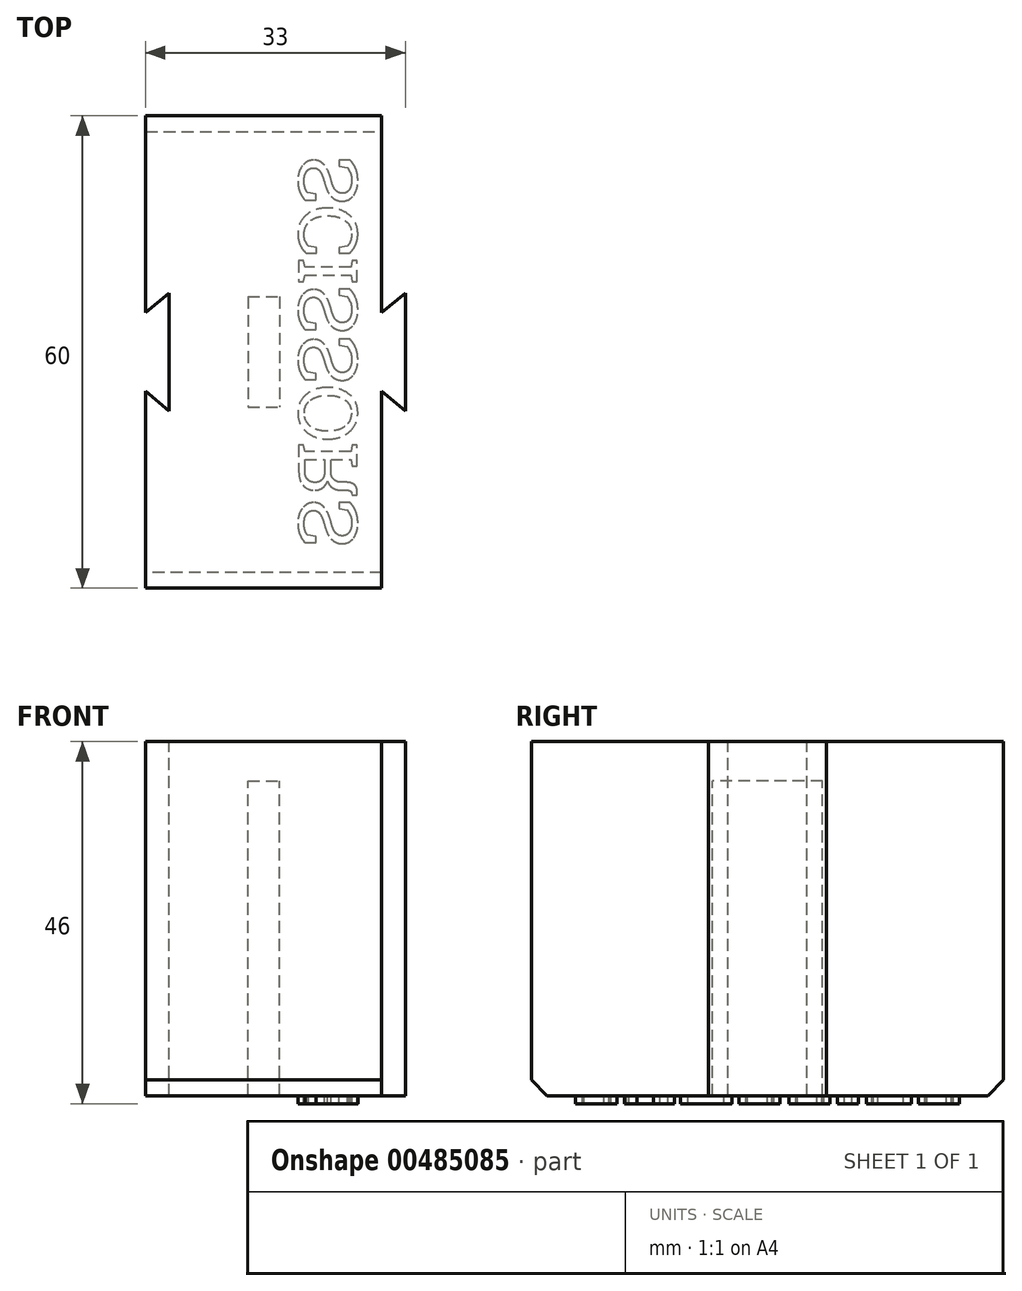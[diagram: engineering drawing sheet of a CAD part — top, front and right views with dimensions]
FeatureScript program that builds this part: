
annotation { "Feature Type Name" : "Feature", "Feature Type Description" : "" }
export const myFeature = defineFeature(function(context is Context, id is Id, definition is map)
    precondition{}
    {
        {
            var Q0;
            Q0=qCreatedBy(makeId("Top.planeOp"),FACE);
            var sketch = newSketch(context, id + "F0", { "sketchPlane" : qUnion([Q0])});
            skPoint(sketch, "E0.middle", {"position": v(0, 0) * mm});
            skLineSegment(sketch, "E1.bottom", {"start": v(15, 30) * mm, "end": v(-15, 30) * mm});
            skLineSegment(sketch, "E1.top", {"start": v(15, -30) * mm, "end": v(-15, -30) * mm});
            skLineSegment(sketch, "E2.left", {"start": v(-12, 7.5) * mm, "end": v(-12, -7.5) * mm});
            skLineSegment(sketch, "E3.left", {"start": v(18, 7.5) * mm, "end": v(18, -7.5) * mm});
            skLineSegment(sketch, "E4", {"start": v(-12, 7.5) * mm, "end": v(-15, 5) * mm});
            skLineSegment(sketch, "E5", {"start": v(15, 30) * mm, "end": v(15, 5) * mm});
            skLineSegment(sketch, "E6", {"start": v(15, -5) * mm, "end": v(15, -30) * mm});
            skLineSegment(sketch, "E7", {"start": v(-15, -30) * mm, "end": v(-15, -5) * mm});
            skLineSegment(sketch, "E8", {"start": v(-12, -7.5) * mm, "end": v(-12, 7.5) * mm});
            skLineSegment(sketch, "E9", {"start": v(-15, -5) * mm, "end": v(-12, -7.5) * mm});
            skLineSegment(sketch, "E10", {"start": v(-15, 5) * mm, "end": v(-15, 30) * mm});
            skLineSegment(sketch, "E11", {"start": v(15, 5) * mm, "end": v(18, 7.5) * mm});
            skLineSegment(sketch, "E12", {"start": v(15, -5) * mm, "end": v(18, -7.5) * mm});
            skLineSegment(sketch, "E13.bottom", {"start": v(-2, 7) * mm, "end": v(2, 7) * mm});
            skLineSegment(sketch, "E13.top", {"start": v(-2, -7) * mm, "end": v(2, -7) * mm});
            skLineSegment(sketch, "E13.left", {"start": v(-2, 7) * mm, "end": v(-2, -7) * mm});
            skLineSegment(sketch, "E13.right", {"start": v(2, 7) * mm, "end": v(2, -7) * mm});
            skSolve(sketch);
        }
        {
            var Q0;
            Q0=makeQuery(id+"F0.imprint","IMPRINT",FACE,{"disambiguationData":[TD([[makeQuery(id+"F0.imprint","IMPRINT",EDGE,{"derivedFrom":sQuery(id+"F0.wireOp",EDGE,"E1.bottom")}),1.0]])]});
            extrude(context, id + "F1", {"entities" : qUnion([Q0]), "oppositeDirection" : true, "depth" : 40 * mm});
        }
        {
            var Q0;
            Q0=makeQuery(id+"F0.imprint","IMPRINT",FACE,{"disambiguationData":[TD([[makeQuery(id+"F0.imprint","IMPRINT",EDGE,{"derivedFrom":sQuery(id+"F0.wireOp",EDGE,"E13.bottom")}),-1.0]])]});
            var Q1;
            Q1=makeQuery(id+"F0.imprint","IMPRINT",FACE,{"disambiguationData":[TD([[makeQuery(id+"F0.imprint","IMPRINT",EDGE,{"derivedFrom":sQuery(id+"F0.wireOp",EDGE,"E1.bottom")}),1.0]])]});
            extrude(context, id + "F2", {"entities" : qUnion([Q0, Q1]), "operationType" : NewBodyOperationType.ADD, "depth" : 5 * mm});
        }
        {
            var Q0;
            Q0=makeQuery(id+"F1.opExtrude","CAP_FACE",FACE,{"disambiguationData":[OSD([sQuery(id+"F0.wireOp",EDGE,"E1.bottom"),sQuery(id+"F0.wireOp",EDGE,"E1.top"),sQuery(id+"F0.wireOp",EDGE,"E4"),sQuery(id+"F0.wireOp",EDGE,"E5"),sQuery(id+"F0.wireOp",EDGE,"E3.left"),sQuery(id+"F0.wireOp",EDGE,"E6"),sQuery(id+"F0.wireOp",EDGE,"E7"),sQuery(id+"F0.wireOp",EDGE,"E8"),sQuery(id+"F0.wireOp",EDGE,"E9"),sQuery(id+"F0.wireOp",EDGE,"E10"),sQuery(id+"F0.wireOp",EDGE,"E11"),sQuery(id+"F0.wireOp",EDGE,"E12"),sQuery(id+"F0.wireOp",EDGE,"E13.bottom"),sQuery(id+"F0.wireOp",EDGE,"E13.top"),sQuery(id+"F0.wireOp",EDGE,"E13.left"),sQuery(id+"F0.wireOp",EDGE,"E13.right")])],"isStart":false});
            var sketch = newSketch(context, id + "F3", { "sketchPlane" : qUnion([Q0])});
            skText(sketch, "E14", { "text": "SCISSORS", "fontName": "RobotoSlab-Regular.ttf"});
            const initialGuessF3  = {"E14": [0.01186, -0.025, 0, 1, 0.0075]};
            skSetInitialGuess(sketch, initialGuessF3);
            skSolve(sketch);
        }
        {
            var Q0;
            Q0 = qSketchRegion(id + "F3", true);
            extrude(context, id + "F4", {"entities" : qUnion([Q0]), "operationType" : NewBodyOperationType.ADD, "depth" : 1 * mm});
        }
        {
            var Q0;
            Q0=makeQuery(id+"F1.opExtrude","CAP_EDGE",EDGE,{"disambiguationData":[OSD([sQuery(id+"F0.wireOp",EDGE,"E1.bottom")])],"isStart":false});
            var Q1;
            Q1=makeQuery(id+"F1.opExtrude","CAP_EDGE",EDGE,{"disambiguationData":[OSD([sQuery(id+"F0.wireOp",EDGE,"E1.top")])],"isStart":false});
            chamfer(context, id + "F5", {"entities" : qUnion([Q0, Q1]), "width" : 2 * mm, "tangentPropagation" : true});
        }
    });
